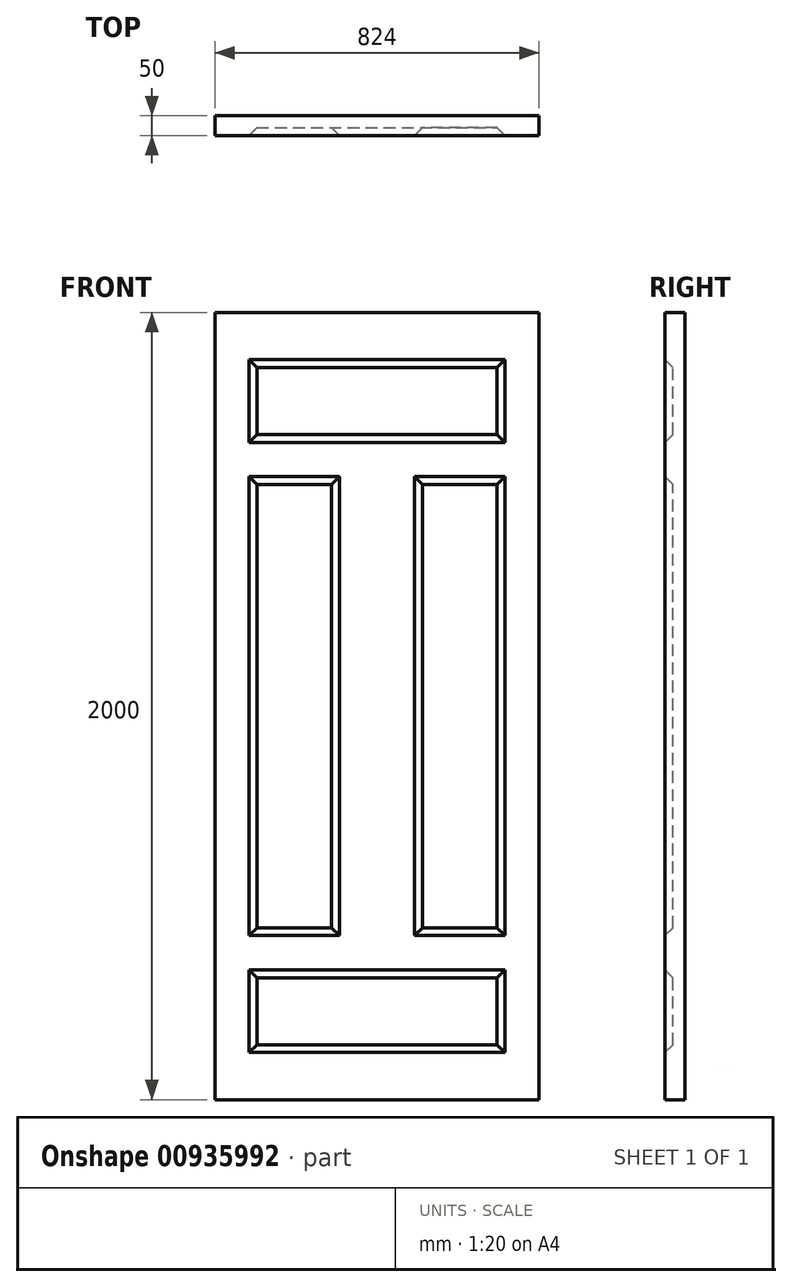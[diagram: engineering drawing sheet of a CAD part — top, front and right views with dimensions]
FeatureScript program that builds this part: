
annotation { "Feature Type Name" : "Feature", "Feature Type Description" : "" }
export const myFeature = defineFeature(function(context is Context, id is Id, definition is map)
    precondition{}
    {
        {
            var Q0;
            Q0=qCreatedBy(makeId("Front.planeOp"),FACE);
            var sketch = newSketch(context, id + "F0", { "sketchPlane" : qUnion([Q0])});
            skLineSegment(sketch, "E0.bottom", {"start": v(412, -1000) * mm, "end": v(-412, -1000) * mm});
            skLineSegment(sketch, "E0.top", {"start": v(412, 1000) * mm, "end": v(-412, 1000) * mm});
            skLineSegment(sketch, "E0.left", {"start": v(412, -1000) * mm, "end": v(412, 1000) * mm});
            skLineSegment(sketch, "E0.right", {"start": v(-412, -1000) * mm, "end": v(-412, 1000) * mm});
            skPoint(sketch, "E0.middle", {"position": v(0, 0) * mm});
            skSolve(sketch);
        }
        {
            var Q0;
            Q0 = qSketchRegion(id + "F0", true);
            extrude(context, id + "F1", {"entities" : qUnion([Q0]), "depth" : 50 * mm, "offsetDistance" : 25 * mm});
        }
        {
            var Q0;
            Q0=makeQuery(id+"F1.opExtrude","CAP_FACE",FACE,{"disambiguationData":[OSD([sQuery(id+"F0.wireOp",EDGE,"E0.bottom"),sQuery(id+"F0.wireOp",EDGE,"E0.top"),sQuery(id+"F0.wireOp",EDGE,"E0.left"),sQuery(id+"F0.wireOp",EDGE,"E0.right")])],"isStart":false});
            var sketch = newSketch(context, id + "F2", { "sketchPlane" : qUnion([Q0])});
            skLineSegment(sketch, "E1", {"start": v(0, 1000) * mm, "end": v(0, -1000) * mm, "construction": true});
            skLineSegment(sketch, "E2.bottom", {"start": v(325, 670) * mm, "end": v(-325, 670) * mm});
            skLineSegment(sketch, "E2.top", {"start": v(325, 880) * mm, "end": v(-325, 880) * mm});
            skLineSegment(sketch, "E2.left", {"start": v(325, 670) * mm, "end": v(325, 880) * mm});
            skLineSegment(sketch, "E2.right", {"start": v(-325, 670) * mm, "end": v(-325, 880) * mm});
            skPoint(sketch, "E2.middle", {"position": v(0, 775) * mm});
            skLineSegment(sketch, "E3.bottom", {"start": v(325, -880) * mm, "end": v(-325, -880) * mm});
            skLineSegment(sketch, "E3.top", {"start": v(325, -670) * mm, "end": v(-325, -670) * mm});
            skLineSegment(sketch, "E3.left", {"start": v(325, -880) * mm, "end": v(325, -670) * mm});
            skLineSegment(sketch, "E3.right", {"start": v(-325, -880) * mm, "end": v(-325, -670) * mm});
            skPoint(sketch, "E3.middle", {"position": v(0, -775) * mm});
            skLineSegment(sketch, "E4", {"start": v(-210, 1000) * mm, "end": v(-210, -1000) * mm, "construction": true});
            skLineSegment(sketch, "E5", {"start": v(210, 1000) * mm, "end": v(210, -1000) * mm, "construction": true});
            skLineSegment(sketch, "E6", {"start": v(-412, 583) * mm, "end": v(412, 583) * mm, "construction": true});
            skLineSegment(sketch, "E7", {"start": v(-325, 1000) * mm, "end": v(-325, -1000) * mm, "construction": true});
            skLineSegment(sketch, "E8", {"start": v(325, -1000) * mm, "end": v(325, 1000) * mm, "construction": true});
            skLineSegment(sketch, "E9.bottom", {"start": v(-325, 583) * mm, "end": v(-95, 583) * mm});
            skLineSegment(sketch, "E9.top", {"start": v(-325, -583) * mm, "end": v(-95, -583) * mm});
            skLineSegment(sketch, "E9.left", {"start": v(-325, 583) * mm, "end": v(-325, -583) * mm});
            skLineSegment(sketch, "E9.right", {"start": v(-95, 583) * mm, "end": v(-95, -583) * mm});
            skPoint(sketch, "E9.middle", {"position": v(-210, 0) * mm});
            skLineSegment(sketch, "E10.bottom", {"start": v(325, 583) * mm, "end": v(95, 583) * mm});
            skLineSegment(sketch, "E10.top", {"start": v(325, -583) * mm, "end": v(95, -583) * mm});
            skLineSegment(sketch, "E10.left", {"start": v(325, 583) * mm, "end": v(325, -583) * mm});
            skLineSegment(sketch, "E10.right", {"start": v(95, 583) * mm, "end": v(95, -583) * mm});
            skPoint(sketch, "E10.middle", {"position": v(210, 0) * mm});
            skSolve(sketch);
        }
        {
            var Q0;
            Q0=makeQuery(id+"F2.imprint","IMPRINT",FACE,{"disambiguationData":[TD([[makeQuery(id+"F2.imprint","IMPRINT",EDGE,{"derivedFrom":sQuery(id+"F2.wireOp",EDGE,"E2.bottom")}),-1.0]])]});
            var Q1;
            Q1=makeQuery(id+"F2.imprint","IMPRINT",FACE,{"disambiguationData":[TD([[makeQuery(id+"F2.imprint","IMPRINT",EDGE,{"derivedFrom":sQuery(id+"F2.wireOp",EDGE,"E9.bottom")}),-1.0]])]});
            var Q2;
            Q2=makeQuery(id+"F2.imprint","IMPRINT",FACE,{"disambiguationData":[TD([[makeQuery(id+"F2.imprint","IMPRINT",EDGE,{"derivedFrom":sQuery(id+"F2.wireOp",EDGE,"E10.bottom")}),1.0]])]});
            var Q3;
            Q3=makeQuery(id+"F2.imprint","IMPRINT",FACE,{"disambiguationData":[TD([[makeQuery(id+"F2.imprint","IMPRINT",EDGE,{"derivedFrom":sQuery(id+"F2.wireOp",EDGE,"E3.bottom")}),-1.0]])]});
            extrude(context, id + "F3", {"entities" : qUnion([Q0, Q1, Q2, Q3]), "operationType" : NewBodyOperationType.REMOVE, "oppositeDirection" : true, "depth" : 20 * mm, "offsetDistance" : 25 * mm});
        }
        {
            var Q0;
            Q0=makeQuery(id+"F3.boolean.opBoolean","COPY",EDGE,{"derivedFrom":makeQuery(id+"F3.opExtrude","CAP_EDGE",EDGE,{"disambiguationData":[OSD([sQuery(id+"F2.wireOp",EDGE,"E9.right")])],"isStart":false})});
            var Q1;
            Q1=makeQuery(id+"F3.boolean.opBoolean","COPY",EDGE,{"derivedFrom":makeQuery(id+"F3.opExtrude","CAP_EDGE",EDGE,{"disambiguationData":[OSD([sQuery(id+"F2.wireOp",EDGE,"E9.bottom")])],"isStart":false})});
            var Q2;
            Q2=makeQuery(id+"F3.boolean.opBoolean","COPY",EDGE,{"derivedFrom":makeQuery(id+"F3.opExtrude","CAP_EDGE",EDGE,{"disambiguationData":[OSD([sQuery(id+"F2.wireOp",EDGE,"E9.left")])],"isStart":false})});
            var Q3;
            Q3=makeQuery(id+"F3.boolean.opBoolean","COPY",EDGE,{"derivedFrom":makeQuery(id+"F3.opExtrude","CAP_EDGE",EDGE,{"disambiguationData":[OSD([sQuery(id+"F2.wireOp",EDGE,"E9.top")])],"isStart":false})});
            var Q4;
            Q4=makeQuery(id+"F3.boolean.opBoolean","COPY",EDGE,{"derivedFrom":makeQuery(id+"F3.opExtrude","CAP_EDGE",EDGE,{"disambiguationData":[OSD([sQuery(id+"F2.wireOp",EDGE,"E10.top")])],"isStart":false})});
            var Q5;
            Q5=makeQuery(id+"F3.boolean.opBoolean","COPY",EDGE,{"derivedFrom":makeQuery(id+"F3.opExtrude","CAP_EDGE",EDGE,{"disambiguationData":[OSD([sQuery(id+"F2.wireOp",EDGE,"E10.right")])],"isStart":false})});
            var Q6;
            Q6=makeQuery(id+"F3.boolean.opBoolean","COPY",EDGE,{"derivedFrom":makeQuery(id+"F3.opExtrude","CAP_EDGE",EDGE,{"disambiguationData":[OSD([sQuery(id+"F2.wireOp",EDGE,"E10.left")])],"isStart":false})});
            var Q7;
            Q7=makeQuery(id+"F3.boolean.opBoolean","COPY",EDGE,{"derivedFrom":makeQuery(id+"F3.opExtrude","CAP_EDGE",EDGE,{"disambiguationData":[OSD([sQuery(id+"F2.wireOp",EDGE,"E10.bottom")])],"isStart":false})});
            var Q8;
            Q8=makeQuery(id+"F3.boolean.opBoolean","COPY",EDGE,{"derivedFrom":makeQuery(id+"F3.opExtrude","CAP_EDGE",EDGE,{"disambiguationData":[OSD([sQuery(id+"F2.wireOp",EDGE,"E2.top")])],"isStart":false})});
            var Q9;
            Q9=makeQuery(id+"F3.boolean.opBoolean","COPY",EDGE,{"derivedFrom":makeQuery(id+"F3.opExtrude","CAP_EDGE",EDGE,{"disambiguationData":[OSD([sQuery(id+"F2.wireOp",EDGE,"E2.right")])],"isStart":false})});
            var Q10;
            Q10=makeQuery(id+"F3.boolean.opBoolean","COPY",EDGE,{"derivedFrom":makeQuery(id+"F3.opExtrude","CAP_EDGE",EDGE,{"disambiguationData":[OSD([sQuery(id+"F2.wireOp",EDGE,"E2.left")])],"isStart":false})});
            var Q11;
            Q11=makeQuery(id+"F3.boolean.opBoolean","COPY",EDGE,{"derivedFrom":makeQuery(id+"F3.opExtrude","CAP_EDGE",EDGE,{"disambiguationData":[OSD([sQuery(id+"F2.wireOp",EDGE,"E2.bottom")])],"isStart":false})});
            var Q12;
            Q12=makeQuery(id+"F3.boolean.opBoolean","COPY",EDGE,{"derivedFrom":makeQuery(id+"F3.opExtrude","CAP_EDGE",EDGE,{"disambiguationData":[OSD([sQuery(id+"F2.wireOp",EDGE,"E3.right")])],"isStart":false})});
            var Q13;
            Q13=makeQuery(id+"F3.boolean.opBoolean","COPY",EDGE,{"derivedFrom":makeQuery(id+"F3.opExtrude","CAP_EDGE",EDGE,{"disambiguationData":[OSD([sQuery(id+"F2.wireOp",EDGE,"E3.bottom")])],"isStart":false})});
            var Q14;
            Q14=makeQuery(id+"F3.boolean.opBoolean","COPY",EDGE,{"derivedFrom":makeQuery(id+"F3.opExtrude","CAP_EDGE",EDGE,{"disambiguationData":[OSD([sQuery(id+"F2.wireOp",EDGE,"E3.left")])],"isStart":false})});
            var Q15;
            Q15=makeQuery(id+"F3.boolean.opBoolean","COPY",EDGE,{"derivedFrom":makeQuery(id+"F3.opExtrude","CAP_EDGE",EDGE,{"disambiguationData":[OSD([sQuery(id+"F2.wireOp",EDGE,"E3.top")])],"isStart":false})});
            chamfer(context, id + "F4", {"entities" : qUnion([Q0, Q1, Q2, Q3, Q4, Q5, Q6, Q7, Q8, Q9, Q10, Q11, Q12, Q13, Q14, Q15]), "width" : 20 * mm, "tangentPropagation" : true});
        }
    });
